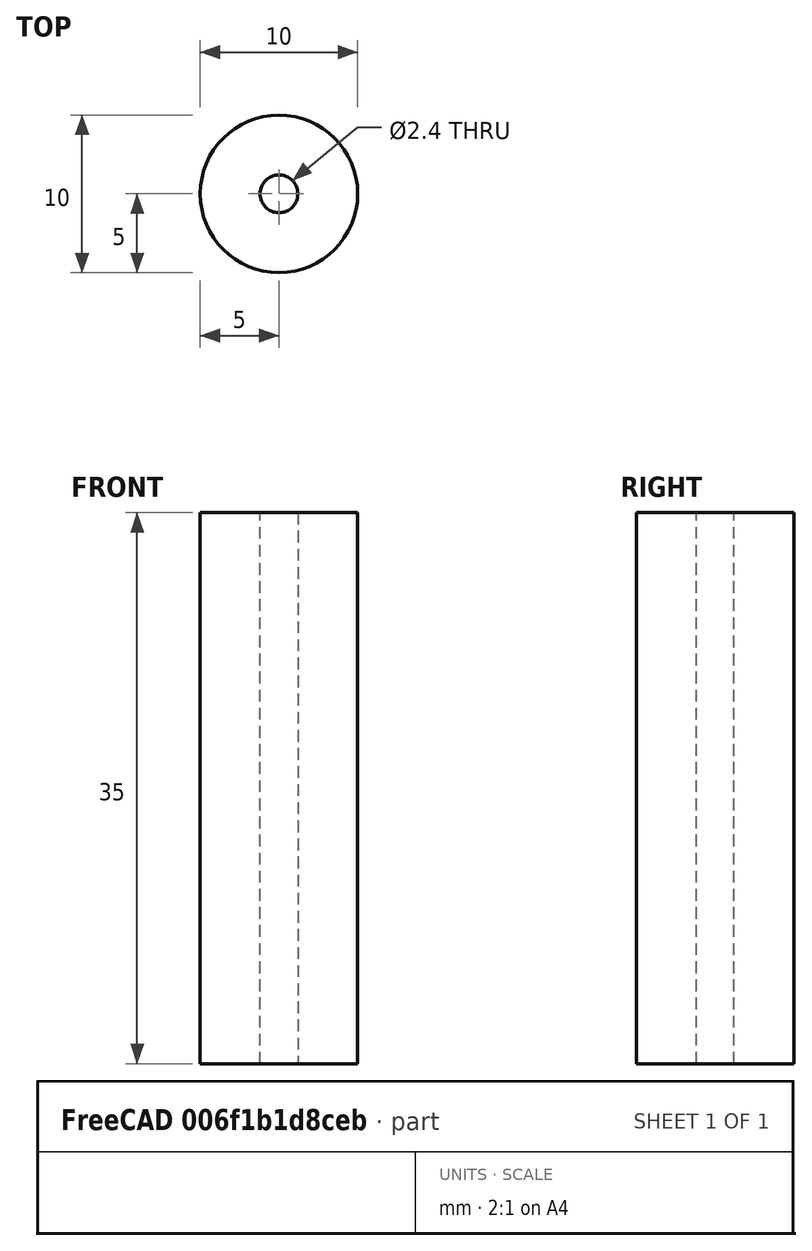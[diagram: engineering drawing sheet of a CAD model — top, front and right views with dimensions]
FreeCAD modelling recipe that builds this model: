
FCSTD DOCUMENT  (FreeCAD 0.21R33668 +26 (Git))
Label: board_connector
License: All rights reserved
LicenseURL: https://en.wikipedia.org/wiki/All_rights_reserved
objects: Sketcher::SketchObject×2, PartDesign::Pad×1, PartDesign::Pocket×1, PartDesign::Body×1
note: 7 computed .brp shape members not serialized (recipe doc carries the construction recipe); baked Part::Feature solids carry a one-line shape summary decoded from their .brp

FEATURE [Sketcher::SketchObject] Sketch
  FullyConstrained = false
  MapMode = 5
  Support = -> [XY_Plane]
  sketch-geometry (2):
    g0: Circle CenterX=0 CenterY=0 CenterZ=0 NormalX=0 NormalY=0 NormalZ=1 AngleXU=0 Radius=5
    g1: GeomPoint X=-3.49712 Y=3.57353 Z=0
  constraints (3):
    c: Coincident(g0,g-1)
    c: PointOnObject(g1,g0)
    c: Distance(g1,g0) = 5
FEATURE [PartDesign::Pad] Pad
  Direction = (0,0,1)
  Length = 35
  Length2 = 10
  Profile = -> Sketch
  ReferenceAxis = -> Sketch [N_Axis]
  Type = 0
FEATURE [Sketcher::SketchObject] Sketch001
  FullyConstrained = false
  MapMode = 5
  Placement = pos=(0,0,35) rot=(0,0,1;0rad)
  Support = -> [Pad]
  sketch-geometry (2):
    g0: Circle CenterX=0 CenterY=0 CenterZ=0 NormalX=0 NormalY=0 NormalZ=1 AngleXU=0 Radius=1.2
    g1: GeomPoint X=-0.940143 Y=0.745742 Z=0
  constraints (3):
    c: Coincident(g0,g-1)
    c: PointOnObject(g1,g0)
    c: Distance(g1,g0) = 1.2
FEATURE [PartDesign::Pocket] Pocket
  BaseFeature = -> Pad
  Direction = (0,0,-1)
  Length = 35
  Length2 = 5
  Profile = -> Sketch001
  ReferenceAxis = -> Sketch001 [N_Axis]
  Type = 0
FEATURE [PartDesign::Body] Body
  Group = -> [Sketch,Pad,Sketch001,Pocket]
  Origin = -> Origin
  Tip = -> Pocket
